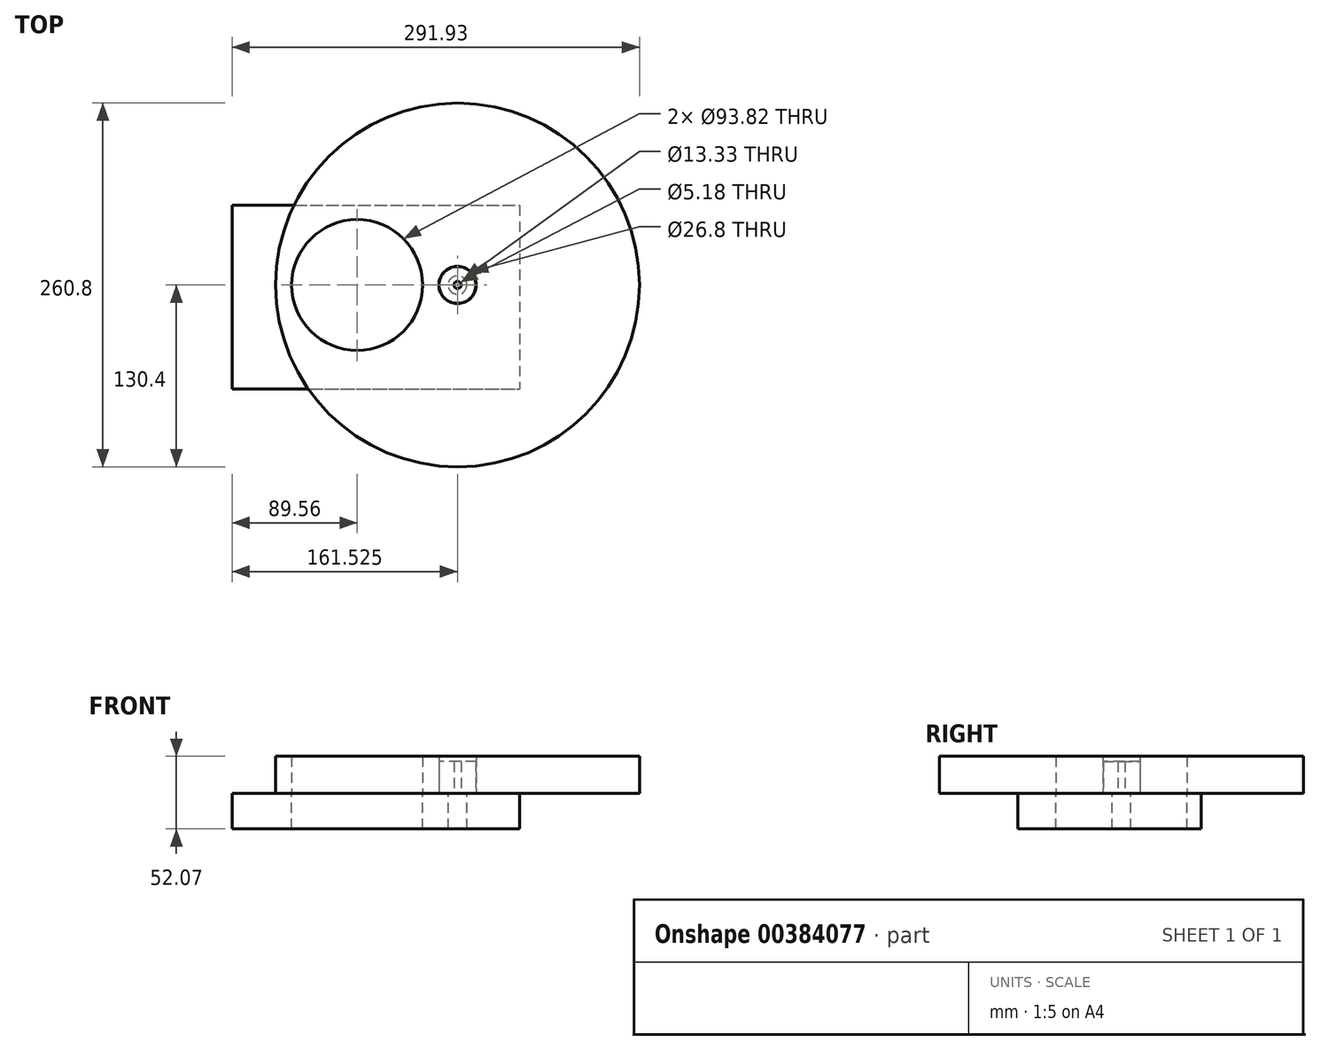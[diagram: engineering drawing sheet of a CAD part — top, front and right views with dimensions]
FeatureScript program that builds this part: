
annotation { "Feature Type Name" : "Feature", "Feature Type Description" : "" }
export const myFeature = defineFeature(function(context is Context, id is Id, definition is map)
    precondition{}
    {
        {
            var Q0;
            Q0=qCreatedBy(makeId("Top.planeOp"),FACE);
            var sketch = newSketch(context, id + "F0", { "sketchPlane" : qUnion([Q0])});
            skLineSegment(sketch, "E0.bottom", {"start": v(-110.97, 57.07) * mm, "end": v(95.13, 57.07) * mm});
            skLineSegment(sketch, "E0.top", {"start": v(-110.97, -74.43) * mm, "end": v(95.13, -74.43) * mm});
            skLineSegment(sketch, "E0.left", {"start": v(-110.97, 57.07) * mm, "end": v(-110.97, -74.43) * mm});
            skLineSegment(sketch, "E0.right", {"start": v(95.13, 57.07) * mm, "end": v(95.13, -74.43) * mm});
            skCircle(sketch, "E1", {"center": v(-21.41, 0) * mm, "radius": 46.91 * mm});
            skCircle(sketch, "E2", {"center": v(50.56, 0) * mm, "radius": 6.67 * mm});
            skCircle(sketch, "E3", {"center": v(50.56, 0) * mm, "radius": 13.18 * mm});
            skCircle(sketch, "E4", {"center": v(50.56, 0) * mm, "radius": 130.4 * mm});
            skCircle(sketch, "E5", {"center": v(50.56, 0) * mm, "radius": 13.4 * mm});
            skCircle(sketch, "E6", {"center": v(50.56, 0) * mm, "radius": 2.6 * mm});
            skSolve(sketch);
        }
        {
            var Q0;
            {var subQ0=sQuery(id+"F0.wireOp",EDGE,"E0.right");Q0=makeQuery(id+"F0.imprint","IMPRINT",FACE,{"disambiguationData":[TD([[makeQuery(id+"F0.imprint","IMPRINT",EDGE,{"derivedFrom":subQ0}),1.0]])]});}
            var Q1;
            {var subQ0=sQuery(id+"F0.wireOp",EDGE,"E0.right");Q1=makeQuery(id+"F0.imprint","IMPRINT",FACE,{"disambiguationData":[TD([[makeQuery(id+"F0.imprint","IMPRINT",EDGE,{"derivedFrom":subQ0}),-1.0]])]});}
            extrude(context, id + "F1", {"entities" : qUnion([Q0, Q1]), "depth" : 26.67 * mm});
        }
        {
            var Q0;
            {var subQ0=sQuery(id+"F0.wireOp",EDGE,"E0.left");Q0=makeQuery(id+"F0.imprint","IMPRINT",FACE,{"disambiguationData":[TD([[makeQuery(id+"F0.imprint","IMPRINT",EDGE,{"derivedFrom":subQ0}),1.0]])]});}
            var Q1;
            {var subQ0=sQuery(id+"F0.wireOp",EDGE,"E0.right");Q1=makeQuery(id+"F0.imprint","IMPRINT",FACE,{"disambiguationData":[TD([[makeQuery(id+"F0.imprint","IMPRINT",EDGE,{"derivedFrom":subQ0}),-1.0]])]});}
            var Q2;
            Q2=makeQuery(id+"F0.imprint","IMPRINT",FACE,{"disambiguationData":[TD([[makeQuery(id+"F0.imprint","IMPRINT",EDGE,{"derivedFrom":sQuery(id+"F0.wireOp",EDGE,"E3")}),-1.0]])]});
            var Q3;
            Q3=makeQuery(id+"F0.imprint","IMPRINT",FACE,{"disambiguationData":[TD([[makeQuery(id+"F0.imprint","IMPRINT",EDGE,{"derivedFrom":sQuery(id+"F0.wireOp",EDGE,"E2")}),-1.0]])]});
            extrude(context, id + "F2", {"entities" : qUnion([Q0, Q1, Q2, Q3]), "oppositeDirection" : true, "depth" : 25.4 * mm});
        }
        {
            var Q0;
            Q0=makeQuery(id+"F0.imprint","IMPRINT",FACE,{"disambiguationData":[TD([[makeQuery(id+"F0.imprint","IMPRINT",EDGE,{"derivedFrom":sQuery(id+"F0.wireOp",EDGE,"E2")}),-1.0]])]});
            var Q1;
            Q1=makeQuery(id+"F0.imprint","IMPRINT",FACE,{"disambiguationData":[TD([[makeQuery(id+"F0.imprint","IMPRINT",EDGE,{"derivedFrom":sQuery(id+"F0.wireOp",EDGE,"E2")}),1.0]])]});
            extrude(context, id + "F3", {"entities" : qUnion([Q0, Q1]), "depth" : 22.86 * mm});
        }
    });
